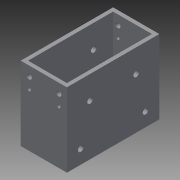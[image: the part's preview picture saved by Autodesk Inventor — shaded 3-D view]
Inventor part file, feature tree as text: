
AUTODESK INVENTOR PART (.ipt)
format: ipt  version: 2013 (Build 170138000, 138)  size: 130,048 bytes
history: native  units: mm
features: sketch x4, hole x3, other x1, extrude x1
ambient origin geometry x8: Origin, YZ Plane, XZ Plane, XY Plane, X Axis, Y Axis, Z Axis, Center Point
feature tree (9):
  other  "ソリッド1"
  extrude  "押し出し1"  Depth=21.0mm
  hole  "穴1"  [1 undecoded]
  hole  "穴2"  [1 undecoded]
  hole  "穴3"  [1 undecoded]
  sketch  "スケッチ1"
  sketch  "スケッチ2"
  sketch  "スケッチ3"
  sketch  "スケッチ4"
note: 3 required parameter values undecoded (feature->parameter linkage not recoverable at this tier; creation-order binding heuristic only, values carry confidence <= 0.55)
